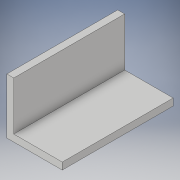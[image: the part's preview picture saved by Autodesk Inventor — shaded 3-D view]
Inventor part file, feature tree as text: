
AUTODESK INVENTOR PART (.ipt)
format: ipt  version: 2018 (Build 220112000, 112)  size: 93,696 bytes
history: native  units: in
note: dims shown in document units (in); Inventor stores cm internally (conversion verified against a paired STEP export)
features: extrude x1, sketch x1
ambient origin geometry x8: Origin, YZ Plane, XZ Plane, XY Plane, X Axis, Y Axis, Z Axis, Center Point
bodies: Solid1 (feature_tree)
feature tree (2):
  extrude  "Extrusion1"  Depth=1.0in
  sketch  "Sketch1"  dims[d0=0.125in d1=1.0in d2=1.0in d3=0.125in d4=2.0in d5=0.0in]
